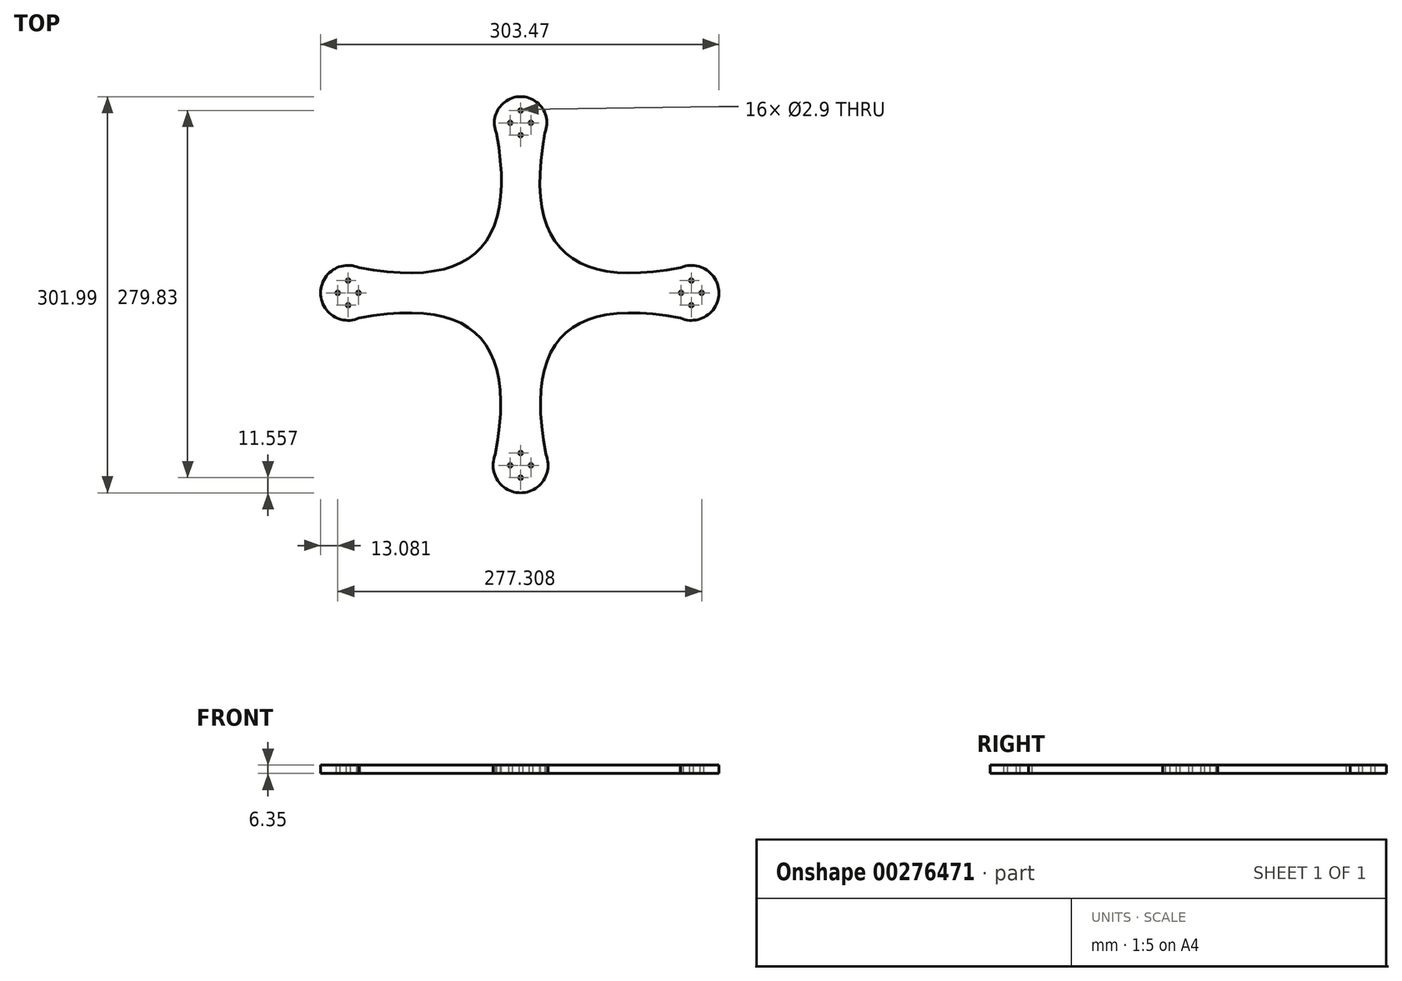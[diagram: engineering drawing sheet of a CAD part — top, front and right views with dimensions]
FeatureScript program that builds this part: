
annotation { "Feature Type Name" : "Feature", "Feature Type Description" : "" }
export const myFeature = defineFeature(function(context is Context, id is Id, definition is map)
    precondition{}
    {
        {
            var Q0;
            Q0=qCreatedBy(makeId("Top.planeOp"),FACE);
            var sketch = newSketch(context, id + "F0", { "sketchPlane" : qUnion([Q0])});
            skLineSegment(sketch, "E0", {"start": v(0, 0) * mm, "end": v(151.07, 0) * mm});
            skLineSegment(sketch, "E1", {"start": v(0, -20.96) * mm, "end": v(0, -152.4) * mm});
            skLineSegment(sketch, "E2", {"start": v(0, 35.81) * mm, "end": v(0, 149.59) * mm});
            skLineSegment(sketch, "E3", {"start": v(0, 149.59) * mm, "end": v(0, 129.59) * mm});
            skCircle(sketch, "E4", {"center": v(0, 129.59) * mm, "radius": 20 * mm});
            skLineSegment(sketch, "E5", {"start": v(0, 129.59) * mm, "end": v(20, 129.59) * mm});
            skLineSegment(sketch, "E6", {"start": v(0, 129.59) * mm, "end": v(-20, 129.59) * mm});
            skLineSegment(sketch, "E7", {"start": v(151.07, 0) * mm, "end": v(130.12, 0) * mm});
            skLineSegment(sketch, "E8", {"start": v(0, -152.4) * mm, "end": v(0, -131.44) * mm});
            skCircle(sketch, "E9", {"center": v(130.12, 0) * mm, "radius": 20.96 * mm});
            skCircle(sketch, "E10", {"center": v(0, -131.44) * mm, "radius": 20.96 * mm});
            skLineSegment(sketch, "E11", {"start": v(130.12, 0) * mm, "end": v(130.12, 20.96) * mm});
            skLineSegment(sketch, "E12", {"start": v(130.12, 20.96) * mm, "end": v(130.12, -20.96) * mm});
            skLineSegment(sketch, "E13", {"start": v(0, -131.44) * mm, "end": v(-20.96, -131.44) * mm});
            skLineSegment(sketch, "E14", {"start": v(-20.96, -131.44) * mm, "end": v(20.96, -131.44) * mm});
            skLineSegment(sketch, "E15", {"start": v(129.4, -20.94) * mm, "end": v(130.12, -20.96) * mm});
            skLineSegment(sketch, "E16.trimOffspring", {"start": v(129.4, 20.94) * mm, "end": v(130.12, 20.95) * mm});
            skLineSegment(sketch, "E17", {"start": v(-35.81, 0) * mm, "end": v(-152.4, 0) * mm});
            skLineSegment(sketch, "E18", {"start": v(-152.4, 0) * mm, "end": v(-131.44, 0) * mm});
            skCircle(sketch, "E19", {"center": v(-131.44, 0) * mm, "radius": 20.96 * mm});
            skLineSegment(sketch, "E20", {"start": v(-131.44, 0) * mm, "end": v(-131.44, 20.96) * mm});
            skLineSegment(sketch, "E21", {"start": v(-131.44, 20.96) * mm, "end": v(-131.44, -20.96) * mm});
            skFitSpline(sketch, "E22", {"points": [v(-131.44, 20.96) * mm, v(-20, 129.59) * mm], "startDerivative": vector(286.9, -62.87) * mm, "endDerivative": vector(-60, 281.32) * mm});
            skFitSpline(sketch, "E23", {"points": [v(20, 129.59) * mm, v(129.4, 20.94) * mm], "startDerivative": vector(-60, -281.32) * mm, "endDerivative": vector(280.79, 62.83) * mm});
            skFitSpline(sketch, "E24", {"points": [v(130.12, -20.96) * mm, v(20.96, -131.44) * mm], "startDerivative": vector(-282.9, 62.87) * mm, "endDerivative": vector(62.87, -286.9) * mm});
            skFitSpline(sketch, "E25", {"points": [v(-20.96, -131.44) * mm, v(-131.44, -20.96) * mm], "startDerivative": vector(62.86, 286.9) * mm, "endDerivative": vector(-286.9, -62.87) * mm});
            skLineSegment(sketch, "E26.trimOffspring", {"start": v(-19.03, -122.68) * mm, "end": v(-20.96, -131.45) * mm});
            skLineSegment(sketch, "E27.trimOffspring", {"start": v(20.95, -131.3) * mm, "end": v(20.96, -131.45) * mm});
            skLineSegment(sketch, "E28", {"start": v(-131.44, 0) * mm, "end": v(-131.44, 9.4) * mm});
            skLineSegment(sketch, "E29", {"start": v(-131.44, 0) * mm, "end": v(-131.44, -9.4) * mm});
            skLineSegment(sketch, "E30", {"start": v(-131.44, 0) * mm, "end": v(-123.57, 0) * mm});
            skLineSegment(sketch, "E31", {"start": v(-131.44, 0) * mm, "end": v(-139.32, 0) * mm});
            skCircle(sketch, "E32", {"center": v(-131.44, 9.4) * mm, "radius": 1.45 * mm});
            skCircle(sketch, "E33", {"center": v(-123.57, 0) * mm, "radius": 1.45 * mm});
            skCircle(sketch, "E34", {"center": v(-131.44, -9.4) * mm, "radius": 1.45 * mm});
            skCircle(sketch, "E35", {"center": v(-139.32, 0) * mm, "radius": 1.45 * mm});
            skLineSegment(sketch, "E36", {"start": v(0, 129.59) * mm, "end": v(0, 138.99) * mm});
            skLineSegment(sketch, "E37", {"start": v(0, 129.59) * mm, "end": v(0, 120.2) * mm});
            skLineSegment(sketch, "E38", {"start": v(0, 129.59) * mm, "end": v(7.87, 129.59) * mm});
            skLineSegment(sketch, "E39", {"start": v(0, 129.59) * mm, "end": v(-7.87, 129.59) * mm});
            skCircle(sketch, "E40", {"center": v(0, 138.99) * mm, "radius": 1.45 * mm});
            skCircle(sketch, "E41", {"center": v(7.87, 129.59) * mm, "radius": 1.45 * mm});
            skCircle(sketch, "E42", {"center": v(0, 120.2) * mm, "radius": 1.45 * mm});
            skCircle(sketch, "E43", {"center": v(-7.87, 129.59) * mm, "radius": 1.45 * mm});
            skLineSegment(sketch, "E44", {"start": v(130.12, 0) * mm, "end": v(130.12, 9.4) * mm});
            skLineSegment(sketch, "E45", {"start": v(130.12, 0) * mm, "end": v(130.12, -9.4) * mm});
            skLineSegment(sketch, "E46", {"start": v(130.12, 0) * mm, "end": v(137.99, 0) * mm});
            skLineSegment(sketch, "E47", {"start": v(130.12, 0) * mm, "end": v(122.24, 0) * mm});
            skCircle(sketch, "E48", {"center": v(122.24, 0) * mm, "radius": 1.45 * mm});
            skCircle(sketch, "E49", {"center": v(130.12, 9.4) * mm, "radius": 1.45 * mm});
            skCircle(sketch, "E50", {"center": v(137.99, 0) * mm, "radius": 1.45 * mm});
            skCircle(sketch, "E51", {"center": v(130.12, -9.4) * mm, "radius": 1.45 * mm});
            skLineSegment(sketch, "E52", {"start": v(0, -131.44) * mm, "end": v(0, -122.05) * mm});
            skLineSegment(sketch, "E53", {"start": v(0, -131.44) * mm, "end": v(0, -140.84) * mm});
            skLineSegment(sketch, "E54", {"start": v(0, -131.44) * mm, "end": v(7.87, -131.44) * mm});
            skLineSegment(sketch, "E55", {"start": v(0, -131.44) * mm, "end": v(-7.87, -131.44) * mm});
            skCircle(sketch, "E56", {"center": v(-7.87, -131.44) * mm, "radius": 1.45 * mm});
            skCircle(sketch, "E57", {"center": v(0, -122.05) * mm, "radius": 1.45 * mm});
            skCircle(sketch, "E58", {"center": v(7.87, -131.44) * mm, "radius": 1.45 * mm});
            skCircle(sketch, "E59", {"center": v(0, -140.84) * mm, "radius": 1.45 * mm});
            skLineSegment(sketch, "E60", {"start": v(0, -20.96) * mm, "end": v(0, -35.81) * mm});
            skLineSegment(sketch, "E61", {"start": v(-25.4, 0) * mm, "end": v(-35.81, 0) * mm});
            skLineSegment(sketch, "E62", {"start": v(0, 0) * mm, "end": v(35.81, 0) * mm});
            skSolve(sketch);
        }
        {
            var Q0;
            Q0 = qSketchRegion(id + "F0", true);
            extrude(context, id + "F1", {"entities" : qUnion([Q0]), "depth" : 6.35 * mm});
        }
    });
